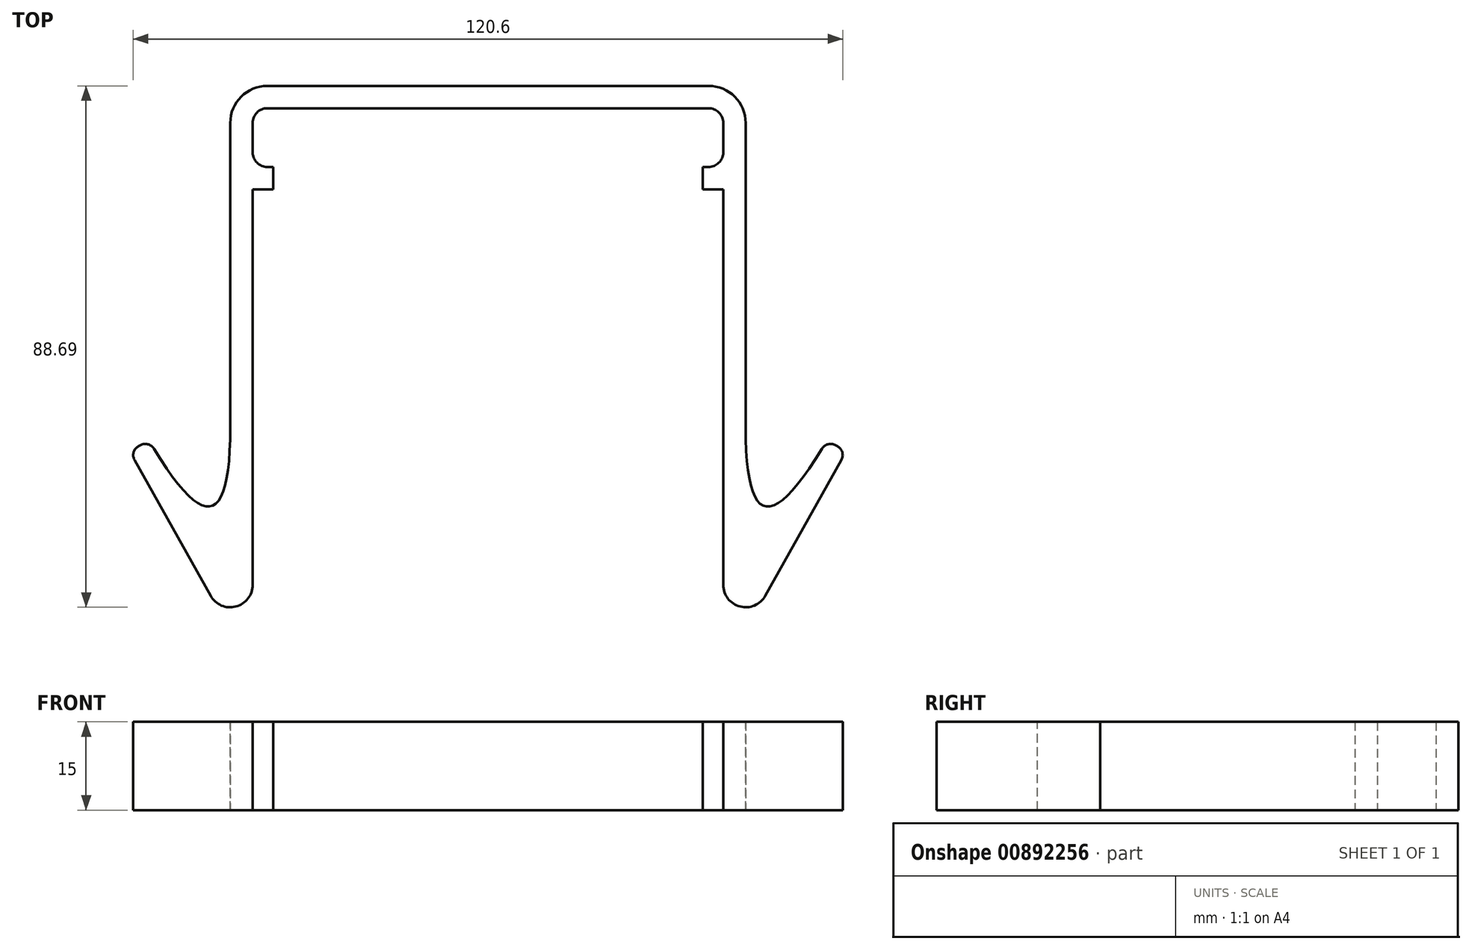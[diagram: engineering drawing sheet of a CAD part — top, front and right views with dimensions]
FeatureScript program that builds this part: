
annotation { "Feature Type Name" : "Feature", "Feature Type Description" : "" }
export const myFeature = defineFeature(function(context is Context, id is Id, definition is map)
    precondition{}
    {
        {
            var Q0;
            Q0=qCreatedBy(makeId("Top.planeOp"),FACE);
            var sketch = newSketch(context, id + "F0", { "sketchPlane" : qUnion([Q0])});
            skLineSegment(sketch, "E0", {"start": v(-37.5, 43.98) * mm, "end": v(0, 43.98) * mm});
            skPoint(sketch, "E1.visualSharp", {"position": v(-40, 43.98) * mm});
            skArc(sketch, "E1.filletArc", {"start": v(-37.5, 43.98) * mm, "mid": v(-39.27, 43.24) * mm, "end": v(-40, 41.48) * mm});
            skArc(sketch, "E2.filletArc", {"start": v(-40, 36.48) * mm, "mid": v(-39.27, 34.7) * mm, "end": v(-37.5, 33.98) * mm});
            skLineSegment(sketch, "E3", {"start": v(-37.5, 47.78) * mm, "end": v(0, 47.78) * mm});
            skLineSegment(sketch, "E4", {"start": v(-43.81, 41.47) * mm, "end": v(-43.81, 36.48) * mm});
            skPoint(sketch, "E5.visualSharp", {"position": v(-43.81, 47.78) * mm});
            skArc(sketch, "E5.filletArc", {"start": v(-37.5, 47.78) * mm, "mid": v(-41.96, 45.93) * mm, "end": v(-43.8, 41.47) * mm});
            skLineSegment(sketch, "E6", {"start": v(-37.5, 33.98) * mm, "end": v(-36.5, 33.98) * mm});
            skLineSegment(sketch, "E7", {"start": v(-37.5, 30.17) * mm, "end": v(-36.5, 30.17) * mm});
            skLineSegment(sketch, "E8", {"start": v(-36.5, 30.17) * mm, "end": v(-36.5, 33.98) * mm});
            skLineSegment(sketch, "E9.MirrorCS", {"start": v(-59.25, -13.44) * mm, "end": v(-59.43, -13.54) * mm});
            skLineSegment(sketch, "E10.MirrorCS", {"start": v(-59.07, -13.34) * mm, "end": v(-59.25, -13.44) * mm});
            skArc(sketch, "E11.MirrorCS", {"start": v(-60.08, -15.86) * mm, "mid": v(-60.24, -14.57) * mm, "end": v(-59.43, -13.54) * mm});
            skArc(sketch, "E12.MirrorCS", {"start": v(-59.07, -13.34) * mm, "mid": v(-57.78, -13.2) * mm, "end": v(-56.76, -14) * mm});
            skLineSegment(sketch, "E13.MirrorCS", {"start": v(-60.08, -15.86) * mm, "end": v(-59.7, -16.55) * mm});
            skLineSegment(sketch, "E14.MirrorCS", {"start": v(-56.37, -14.7) * mm, "end": v(-56.76, -14) * mm});
            skArc(sketch, "E15.MirrorCS", {"start": v(-40, 41.48) * mm, "mid": v(-39.27, 43.24) * mm, "end": v(-37.5, 43.98) * mm});
            skLineSegment(sketch, "E16.MirrorCS", {"start": v(0, 43.98) * mm, "end": v(-37.5, 43.98) * mm});
            skPoint(sketch, "E17.MirrorP", {"position": v(-57.6, -12.51) * mm});
            skLineSegment(sketch, "E18.MirrorCS", {"start": v(-48.5, -28.75) * mm, "end": v(-56.37, -14.7) * mm});
            skLineSegment(sketch, "E19.MirrorCS", {"start": v(0, 47.78) * mm, "end": v(-37.5, 47.78) * mm});
            skPoint(sketch, "E20.MirrorP", {"position": v(-43.81, -37.1) * mm});
            skPoint(sketch, "E21.MirrorP", {"position": v(-40, -51.7) * mm});
            skLineSegment(sketch, "E22.MirrorCS", {"start": v(-59.7, -16.55) * mm, "end": v(-47.13, -38.97) * mm});
            skLineSegment(sketch, "E23.MirrorCS", {"start": v(-40, -37.1) * mm, "end": v(-40, -37.1) * mm});
            skPoint(sketch, "E24.MirrorP", {"position": v(-60.91, -14.38) * mm});
            skLineSegment(sketch, "E25.MirrorCS", {"start": v(-43.81, 41.47) * mm, "end": v(-43.81, -27.53) * mm});
            skArc(sketch, "E26.MirrorCS", {"start": v(-40, -37.1) * mm, "mid": v(-42.85, -40.8) * mm, "end": v(-47.13, -38.97) * mm});
            skArc(sketch, "E27.MirrorCS", {"start": v(-43.8, 41.47) * mm, "mid": v(-41.96, 45.93) * mm, "end": v(-37.5, 47.78) * mm});
            skLineSegment(sketch, "E28.MirrorCS", {"start": v(-40, 41.48) * mm, "end": v(-40, 36.48) * mm});
            skLineSegment(sketch, "E29", {"start": v(-40, 30.17) * mm, "end": v(-40, -37.1) * mm});
            skPoint(sketch, "E30", {"position": v(-40, 30.17) * mm});
            skLineSegment(sketch, "E31", {"start": v(-40, 30.17) * mm, "end": v(-37.5, 30.17) * mm});
            skLineSegment(sketch, "E32", {"start": v(-43.81, -27.53) * mm, "end": v(-43.81, -37.1) * mm});
            skLineSegment(sketch, "E33", {"start": v(0, 47.78) * mm, "end": v(0, 43.98) * mm});
            skLineSegment(sketch, "E34", {"start": v(-48.5, -28.75) * mm, "end": v(-43.81, -37.1) * mm});
            skSolve(sketch);
        }
        {
            var Q0;
            Q0=makeQuery(id+"F0.imprint","IMPRINT",FACE,{"disambiguationData":[TD([[makeQuery(id+"F0.imprint","IMPRINT",EDGE,{"derivedFrom":sQuery(id+"F0.wireOp",EDGE,"E2.filletArc")}),-1.0]])]});
            extrude(context, id + "F1", {"entities" : qUnion([Q0]), "depth" : 15 * mm, "offsetDistance" : 25 * mm});
        }
        {
            var Q0;
            Q0=makeQuery(id+"F1.opExtrude","SWEPT_EDGE",EDGE,{"disambiguationData":[OSD([sQuery(id+"F0.wireOp",EDGE,"E32"),sQuery(id+"F0.wireOp",EDGE,"E34")])]});
            fillet(context, id + "F2", {"entities" : qUnion([Q0]), "tangentPropagation" : true, "crossSection" : FilletCrossSection.CONIC, "radius" : 7 * mm, "rho" : 0.5, "defaultsChanged" : false, "vertexSettings" : [], "allowEdgeOverflow" : false});
        }
        {
            var Q0;
            Q0=makeQuery(id+"F1.opExtrude","SWEPT_BODY",BODY,{"disambiguationData":[OSD([sQuery(id+"F0.wireOp",EDGE,"E2.filletArc"),sQuery(id+"F0.wireOp",EDGE,"E6"),sQuery(id+"F0.wireOp",EDGE,"E7"),sQuery(id+"F0.wireOp",EDGE,"E8"),sQuery(id+"F0.wireOp",EDGE,"E9.MirrorCS"),sQuery(id+"F0.wireOp",EDGE,"E10.MirrorCS"),sQuery(id+"F0.wireOp",EDGE,"E11.MirrorCS"),sQuery(id+"F0.wireOp",EDGE,"E12.MirrorCS"),sQuery(id+"F0.wireOp",EDGE,"E13.MirrorCS"),sQuery(id+"F0.wireOp",EDGE,"E14.MirrorCS"),sQuery(id+"F0.wireOp",EDGE,"E15.MirrorCS"),sQuery(id+"F0.wireOp",EDGE,"E16.MirrorCS"),sQuery(id+"F0.wireOp",EDGE,"E18.MirrorCS"),sQuery(id+"F0.wireOp",EDGE,"E19.MirrorCS"),sQuery(id+"F0.wireOp",EDGE,"E22.MirrorCS"),sQuery(id+"F0.wireOp",EDGE,"E25.MirrorCS"),sQuery(id+"F0.wireOp",EDGE,"E26.MirrorCS"),sQuery(id+"F0.wireOp",EDGE,"E27.MirrorCS"),sQuery(id+"F0.wireOp",EDGE,"E28.MirrorCS"),sQuery(id+"F0.wireOp",EDGE,"E29"),sQuery(id+"F0.wireOp",EDGE,"E31"),sQuery(id+"F0.wireOp",EDGE,"E32"),sQuery(id+"F0.wireOp",EDGE,"E33"),sQuery(id+"F0.wireOp",EDGE,"E34")])]});
            var Q1;
            Q1=makeQuery(id+"F1.opExtrude","SWEPT_FACE",FACE,{"disambiguationData":[OSD([sQuery(id+"F0.wireOp",EDGE,"E33")])]});
            mirror(context, id + "F3", {"operationType" : NewBodyOperationType.ADD, "entities" : qUnion([Q0]), "mirrorPlane" : qUnion([Q1])});
        }
    });
